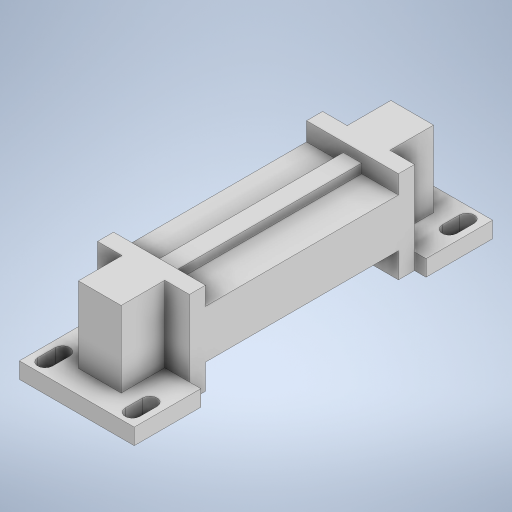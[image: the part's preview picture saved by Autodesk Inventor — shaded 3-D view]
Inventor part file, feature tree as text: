
AUTODESK INVENTOR PART (.ipt)
format: ipt  version: 2024 (Build 280153000, 153)  size: 366,080 bytes
history: native  units: in
note: dims shown in document units (in); Inventor stores cm internally (conversion verified against a paired STEP export)
features: extrude x6, sketch x6
ambient origin geometry x8: Origin, YZ Plane, XZ Plane, XY Plane, X Axis, Y Axis, Z Axis, Center Point
bodies: Solid1 (feature_tree)
feature tree (12):
  extrude  "Extrusion1"  Depth=3.9in
  extrude  "Extrusion2"  TaperAngle=90.0deg  [1 undecoded]
  extrude  "Extrusion3"  TaperAngle=90.0deg  [1 undecoded]
  extrude  "Extrusion4"  TaperAngle=90.0deg  [1 undecoded]
  extrude  "Extrusion5"  TaperAngle=90.0deg  [1 undecoded]
  extrude  "Extrusion6"  Depth=0.4in
  sketch  "Sketch1"  dims[d0=1.25in d1=3.9in]
  sketch  "Sketch2"  dims[d2=0.05in d3=90.0deg]
  sketch  "Sketch3"  dims[d4=0.05in d5=90.0deg]
  sketch  "Sketch4"  dims[d6=0.07in d7=90.0deg]
  sketch  "Sketch5"  dims[d8=0.07in d9=90.0deg]
  sketch  "Sketch6"  dims[d10=0.4in d11=0.4in d12=0.08in d13=0.08in d14=0.175in d15=0.0in d16=2.45in d17=0.175in d18=0.0in d19=1.0in d20=2.1in d21=0.825in d22=0.0in d23=0.325in d24=0.325in d25=0.465in d26=0.1in d27=0.0in d28=0.2in d29=0.1in d30=0.0in d31=0.2in d32=0.1in d33=0.0in]
note: 4 required parameter values undecoded (feature->parameter linkage not recoverable at this tier; creation-order binding heuristic only, values carry confidence <= 0.55)
